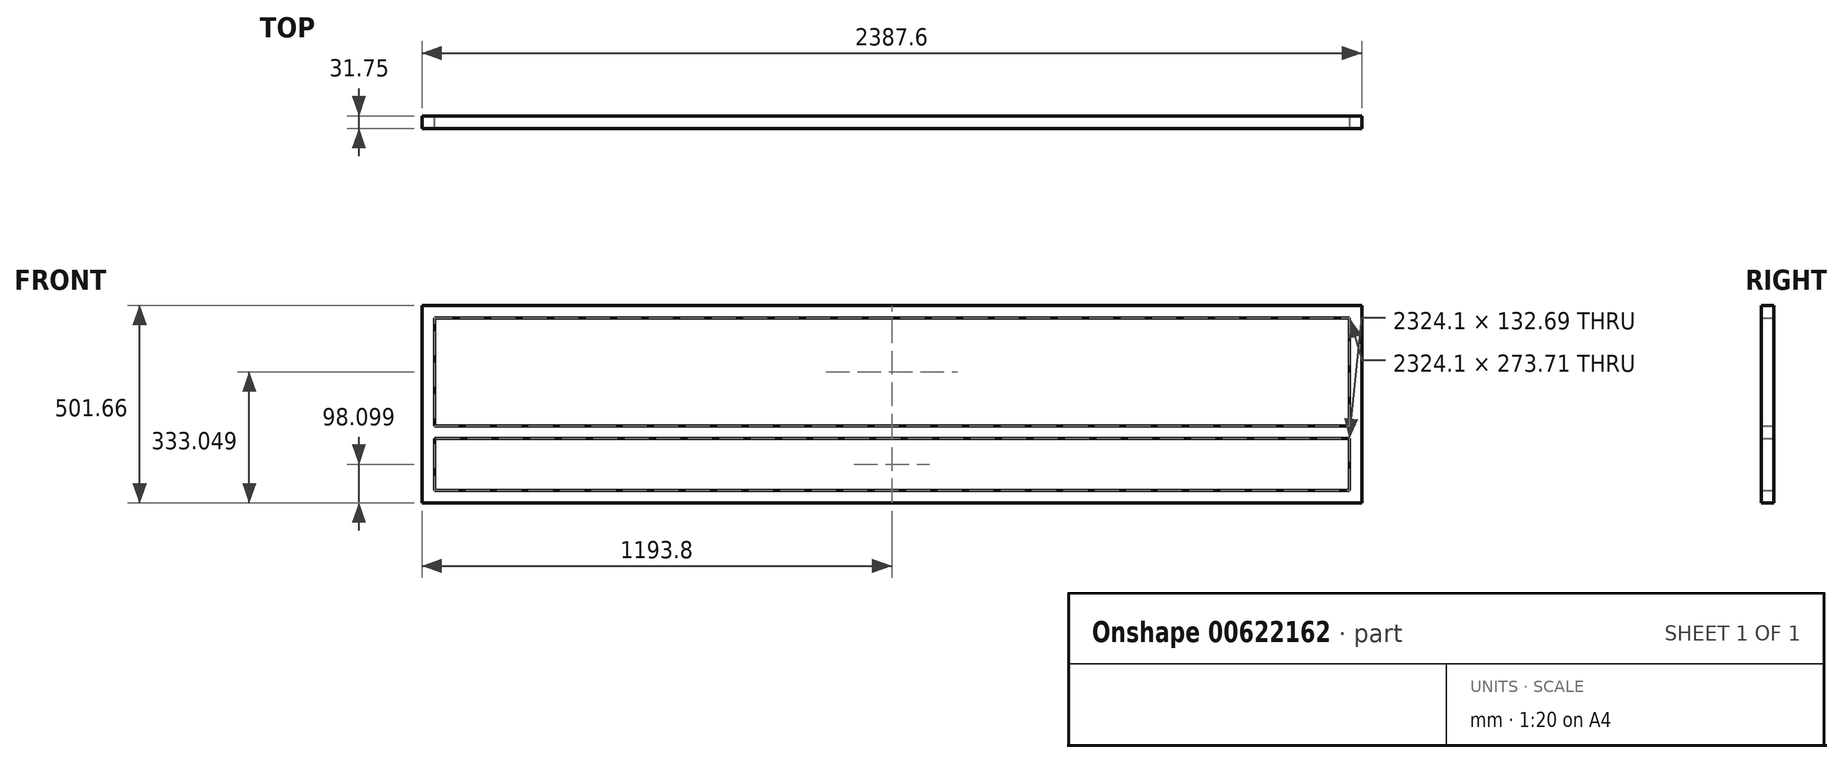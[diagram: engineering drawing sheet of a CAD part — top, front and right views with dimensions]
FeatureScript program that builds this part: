
annotation { "Feature Type Name" : "Feature", "Feature Type Description" : "" }
export const myFeature = defineFeature(function(context is Context, id is Id, definition is map)
    precondition{}
    {
        {
            var Q0;
            Q0=qCreatedBy(makeId("Front.planeOp"),FACE);
            var sketch = newSketch(context, id + "F0", { "sketchPlane" : qUnion([Q0])});
            skLineSegment(sketch, "E0.bottom", {"start": v(1193.8, -15.87) * mm, "end": v(-1193.8, -15.88) * mm});
            skLineSegment(sketch, "E0.top", {"start": v(1193.8, 15.88) * mm, "end": v(-1193.8, 15.88) * mm});
            skLineSegment(sketch, "E0.left", {"start": v(1193.8, -15.87) * mm, "end": v(1193.8, 15.88) * mm});
            skLineSegment(sketch, "E0.right", {"start": v(-1193.8, -15.88) * mm, "end": v(-1193.8, 15.87) * mm});
            skPoint(sketch, "E0.middle", {"position": v(0, 0) * mm});
            skSolve(sketch);
        }
        {
            var Q0;
            Q0 = qSketchRegion(id + "F0", true);
            extrude(context, id + "F1", {"entities" : qUnion([Q0]), "depth" : 31.75 * mm, "offsetDistance" : 25.4 * mm});
        }
        {
            var Q0;
            Q0=makeQuery(id+"F1.opExtrude","SWEPT_FACE",FACE,{"disambiguationData":[OSD([sQuery(id+"F0.wireOp",EDGE,"E0.top")])]});
            var sketch = newSketch(context, id + "F2", { "sketchPlane" : qUnion([Q0])});
            skLineSegment(sketch, "E1.bottom", {"start": v(-1193.8, -31.75) * mm, "end": v(-1162.05, -31.75) * mm});
            skLineSegment(sketch, "E1.top", {"start": v(-1193.8, 0) * mm, "end": v(-1162.05, 0) * mm});
            skLineSegment(sketch, "E1.left", {"start": v(-1193.8, -31.75) * mm, "end": v(-1193.8, 0) * mm});
            skLineSegment(sketch, "E1.right", {"start": v(-1162.05, -31.75) * mm, "end": v(-1162.05, 0) * mm});
            skSolve(sketch);
        }
        {
            var Q0;
            Q0 = qSketchRegion(id + "F2", true);
            extrude(context, id + "F3", {"entities" : qUnion([Q0]), "operationType" : NewBodyOperationType.ADD, "depth" : 469.9 * mm, "offsetDistance" : 25.4 * mm});
        }
        {
            var Q0;
            Q0=makeQuery(id+"F3.opExtrude","SWEPT_FACE",FACE,{"disambiguationData":[OSD([sQuery(id+"F2.wireOp",EDGE,"E1.right")])]});
            var sketch = newSketch(context, id + "F4", { "sketchPlane" : qUnion([Q0])});
            skLineSegment(sketch, "E2.bottom", {"start": v(-31.75, 485.78) * mm, "end": v(0, 485.78) * mm});
            skLineSegment(sketch, "E2.top", {"start": v(-31.75, 454.03) * mm, "end": v(0, 454.03) * mm});
            skLineSegment(sketch, "E2.left", {"start": v(-31.75, 485.78) * mm, "end": v(-31.75, 454.03) * mm});
            skLineSegment(sketch, "E2.right", {"start": v(0, 485.78) * mm, "end": v(0, 454.03) * mm});
            skSolve(sketch);
        }
        {
            var Q0;
            Q0 = qSketchRegion(id + "F4", true);
            extrude(context, id + "F5", {"entities" : qUnion([Q0]), "operationType" : NewBodyOperationType.ADD, "depth" : 2355.85 * mm, "offsetDistance" : 25.4 * mm});
        }
        {
            var Q0;
            Q0=makeQuery(id+"F5.boolean.opBoolean","MERGE",FACE,{"derivedFrom":[makeQuery(id+"F3.opExtrude","CAP_FACE",FACE,{"disambiguationData":[OSD([sQuery(id+"F2.wireOp",EDGE,"E1.bottom"),sQuery(id+"F2.wireOp",EDGE,"E1.top"),sQuery(id+"F2.wireOp",EDGE,"E1.left"),sQuery(id+"F2.wireOp",EDGE,"E1.right")])],"isStart":false}),makeQuery(id+"F5.opExtrude","SWEPT_FACE",FACE,{"disambiguationData":[OSD([sQuery(id+"F4.wireOp",EDGE,"E2.bottom")])]})]});
            var sketch = newSketch(context, id + "F6", { "sketchPlane" : qUnion([Q0])});
            skLineSegment(sketch, "E3.bottom", {"start": v(1193.8, -31.75) * mm, "end": v(1162.05, -31.75) * mm});
            skLineSegment(sketch, "E3.top", {"start": v(1193.8, 0) * mm, "end": v(1162.05, 0) * mm});
            skLineSegment(sketch, "E3.left", {"start": v(1193.8, -31.75) * mm, "end": v(1193.8, 0) * mm});
            skLineSegment(sketch, "E3.right", {"start": v(1162.05, -31.75) * mm, "end": v(1162.05, 0) * mm});
            skSolve(sketch);
        }
        {
            var Q0;
            Q0 = qSketchRegion(id + "F6", true);
            extrude(context, id + "F7", {"entities" : qUnion([Q0]), "operationType" : NewBodyOperationType.ADD, "oppositeDirection" : true, "depth" : 501.65 * mm, "offsetDistance" : 25.4 * mm});
        }
        {
            var Q0;
            Q0=makeQuery(id+"F3.opExtrude","SWEPT_FACE",FACE,{"disambiguationData":[OSD([sQuery(id+"F2.wireOp",EDGE,"E1.right")])]});
            var sketch = newSketch(context, id + "F8", { "sketchPlane" : qUnion([Q0])});
            skLineSegment(sketch, "E4.bottom", {"start": v(-31.75, 148.56) * mm, "end": v(0, 148.56) * mm});
            skLineSegment(sketch, "E4.top", {"start": v(-31.75, 180.31) * mm, "end": v(0, 180.31) * mm});
            skLineSegment(sketch, "E4.left", {"start": v(-31.75, 148.56) * mm, "end": v(-31.75, 180.31) * mm});
            skLineSegment(sketch, "E4.right", {"start": v(0, 148.56) * mm, "end": v(0, 180.31) * mm});
            skSolve(sketch);
        }
        {
            var Q0;
            Q0 = qSketchRegion(id + "F8", true);
            extrude(context, id + "F9", {"entities" : qUnion([Q0]), "operationType" : NewBodyOperationType.ADD, "depth" : 2336.8 * mm, "offsetDistance" : 25.4 * mm});
        }
    });
